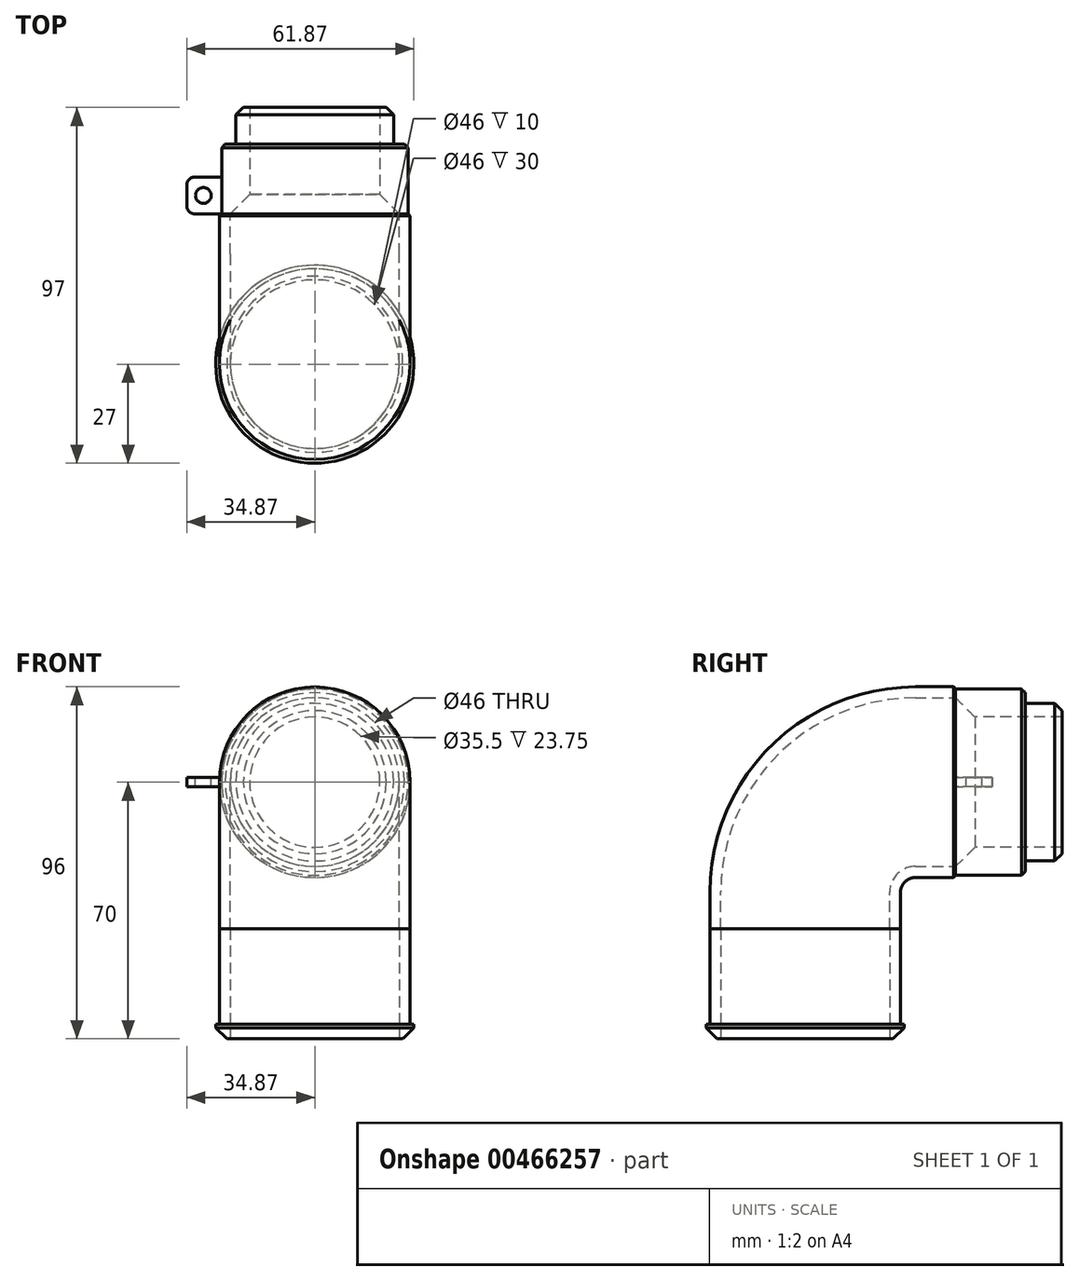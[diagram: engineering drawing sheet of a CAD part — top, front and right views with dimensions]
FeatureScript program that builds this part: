
annotation { "Feature Type Name" : "Feature", "Feature Type Description" : "" }
export const myFeature = defineFeature(function(context is Context, id is Id, definition is map)
    precondition{}
    {
        {
            assignVariable(context, id + "F0", {"name" : "Cyclone_OD", "anyValue" : 52});
        }
        {
            assignVariable(context, id + "F1", {"name" : "Cyclone_ID", "anyValue" : getVariable(context, 'Cyclone_OD') - 6});
        }
        {
            assignVariable(context, id + "F2", {"name" : "CentralVac_ID", "anyValue" : 35.5});
        }
        {
            assignVariable(context, id + "F3", {"name" : "CentralVac_OD1", "anyValue" : 50.8});
        }
        {
            var Q0;
            Q0=qCreatedBy(makeId("Top.planeOp"),FACE);
            var sketch = newSketch(context, id + "F4", { "sketchPlane" : qUnion([Q0])});
            skCircle(sketch, "E0", {"center": v(0, 0) * mm, "radius": 23 * mm});
            skCircle(sketch, "E1", {"center": v(0, 0) * mm, "radius": 26 * mm});
            skSolve(sketch);
        }
        {
            var Q0;
            Q0 = qSketchRegion(id + "F4", true);
            extrude(context, id + "F5", {"entities" : qUnion([Q0]), "depth" : 30 * mm});
        }
        {
            var Q0;
            Q0=makeQuery(id+"F5.opExtrude","CAP_FACE",FACE,{"disambiguationData":[OSD([sQuery(id+"F4.wireOp",EDGE,"E0"),sQuery(id+"F4.wireOp",EDGE,"E1")])],"isStart":true});
            var sketch = newSketch(context, id + "F6", { "sketchPlane" : qUnion([Q0])});
            skCircle(sketch, "E2", {"center": v(0, 0) * mm, "radius": 26 * mm});
            skCircle(sketch, "E3", {"center": v(0, 0) * mm, "radius": 27 * mm});
            skSolve(sketch);
        }
        {
            var Q0;
            Q0 = qSketchRegion(id + "F6", true);
            extrude(context, id + "F7", {"entities" : qUnion([Q0]), "operationType" : NewBodyOperationType.ADD, "depth" : -4 * mm});
        }
        {
            var Q0;
            Q0=makeQuery(id+"F7.opExtrude","CAP_EDGE",EDGE,{"disambiguationData":[OSD([sQuery(id+"F6.wireOp",EDGE,"E3")])],"isStart":true});
            chamfer(context, id + "F8", {"entities" : qUnion([Q0]), "width" : 3 * mm, "tangentPropagation" : true});
        }
        {
            var Q0;
            Q0=qCreatedBy(makeId("Right.planeOp"),FACE);
            var sketch = newSketch(context, id + "F9", { "sketchPlane" : qUnion([Q0])});
            skLineSegment(sketch, "E4", {"start": v(41, 70) * mm, "end": v(41, 30) * mm, "construction": true});
            skLineSegment(sketch, "E5", {"start": v(41, 30) * mm, "end": v(26, 30) * mm, "construction": true});
            skLineSegment(sketch, "E6", {"start": v(41, 70) * mm, "end": v(30, 70) * mm});
            skLineSegment(sketch, "E7", {"start": v(0, 40) * mm, "end": v(0, 30) * mm});
            skPoint(sketch, "E8.visualSharp", {"position": v(0, 70) * mm});
            skArc(sketch, "E8.filletArc", {"start": v(30, 70) * mm, "mid": v(8.79, 61.21) * mm, "end": v(0, 40) * mm});
            skSolve(sketch);
        }
        {
            var Q0;
            Q0=makeQuery(id+"F5.opExtrude","CAP_FACE",FACE,{"disambiguationData":[OSD([sQuery(id+"F4.wireOp",EDGE,"E0"),sQuery(id+"F4.wireOp",EDGE,"E1")])],"isStart":false});
            var sketch = newSketch(context, id + "F10", { "sketchPlane" : qUnion([Q0])});
            skCircle(sketch, "E9", {"center": v(0, 0) * mm, "radius": 23 * mm});
            skCircle(sketch, "E10", {"center": v(0, 0) * mm, "radius": 26 * mm});
            skSolve(sketch);
        }
        {
            var Q0;
            Q0 = qSketchRegion(id + "F10", true);
            var Q1;
            Q1 = qConstructionFilter(qBodyType(qCreatedBy(id + "F9" ,EDGE), BodyType.WIRE), ConstructionObject.NO);
            sweep(context, id + "F11", {"profiles" : qUnion([Q0]), "path" : qUnion([Q1])});
        }
        {
            var Q0;
            Q0=makeQuery(id+"F11.opSweep","CAP_FACE",FACE,{"disambiguationData":[OSD([sQuery(id+"F9.wireOp",VERTEX,"E6.start"),sQuery(id+"F10.wireOp",EDGE,"E9"),sQuery(id+"F10.wireOp",EDGE,"E10")])],"isStart":false});
            var sketch = newSketch(context, id + "F12", { "sketchPlane" : qUnion([Q0])});
            skCircle(sketch, "E11", {"center": v(0, 70) * mm, "radius": 25.4 * mm});
            skCircle(sketch, "E12", {"center": v(0, 70) * mm, "radius": 17.75 * mm});
            skSolve(sketch);
        }
        {
            var Q0;
            Q0 = qSketchRegion(id + "F12", true);
            extrude(context, id + "F13", {"entities" : qUnion([Q0]), "depth" : 19 * mm});
        }
        {
            var Q0;
            Q0=makeQuery(id+"F13.opExtrude","CAP_FACE",FACE,{"disambiguationData":[OSD([sQuery(id+"F12.wireOp",EDGE,"E11"),sQuery(id+"F12.wireOp",EDGE,"E12")])],"isStart":false});
            var sketch = newSketch(context, id + "F14", { "sketchPlane" : qUnion([Q0])});
            skCircle(sketch, "E13", {"center": v(0, 70) * mm, "radius": 17.75 * mm});
            skCircle(sketch, "E14", {"center": v(0, 70) * mm, "radius": 21.5 * mm});
            skSolve(sketch);
        }
        {
            var Q0;
            Q0 = qSketchRegion(id + "F14", true);
            extrude(context, id + "F15", {"entities" : qUnion([Q0]), "operationType" : NewBodyOperationType.ADD, "depth" : 10 * mm});
        }
        {
            var Q0;
            Q0=makeQuery(id+"F13.opExtrude","CAP_EDGE",EDGE,{"disambiguationData":[OSD([sQuery(id+"F12.wireOp",EDGE,"E12")])],"isStart":true});
            chamfer(context, id + "F16", {"entities" : qUnion([Q0]), "width" : ((getVariable(context, 'Cyclone_ID') - getVariable(context, 'CentralVac_ID')) / 2) * mm, "tangentPropagation" : true});
        }
        {
            var Q0;
            Q0=makeQuery(id+"F11.opSweep","CAP_EDGE",EDGE,{"disambiguationData":[OSD([sQuery(id+"F9.wireOp",VERTEX,"E6.start"),sQuery(id+"F10.wireOp",EDGE,"E10")])],"isStart":false});
            chamfer(context, id + "F17", {"entities" : qUnion([Q0]), "width" : ((getVariable(context, 'Cyclone_OD') - getVariable(context, 'CentralVac_OD1')) / 2) * mm, "tangentPropagation" : true});
        }
        {
            var Q0;
            Q0=makeQuery(id+"F15.opExtrude","CAP_EDGE",EDGE,{"disambiguationData":[OSD([sQuery(id+"F14.wireOp",EDGE,"E14")])],"isStart":false});
            chamfer(context, id + "F18", {"entities" : qUnion([Q0]), "width" : 2 * mm, "tangentPropagation" : true});
        }
        {
            var Q0;
            Q0=makeQuery(id+"F13.opExtrude","CAP_EDGE",EDGE,{"disambiguationData":[OSD([sQuery(id+"F12.wireOp",EDGE,"E11")])],"isStart":false});
            chamfer(context, id + "F19", {"entities" : qUnion([Q0]), "width" : 1 * mm, "tangentPropagation" : true});
        }
        {
            var Q0;
            Q0=makeQuery(id+"F13.opExtrude","CAP_FACE",FACE,{"disambiguationData":[OSD([sQuery(id+"F12.wireOp",EDGE,"E11"),sQuery(id+"F12.wireOp",EDGE,"E12")])],"isStart":true});
            var sketch = newSketch(context, id + "F20", { "sketchPlane" : qUnion([Q0])});
            skLineSegment(sketch, "E15.bottom", {"start": v(-34.87, 68.75) * mm, "end": v(-25.37, 68.75) * mm});
            skLineSegment(sketch, "E15.top", {"start": v(-34.87, 71.25) * mm, "end": v(-25.37, 71.25) * mm});
            skLineSegment(sketch, "E15.left", {"start": v(-34.87, 68.75) * mm, "end": v(-34.87, 71.25) * mm});
            skLineSegment(sketch, "E15.right", {"start": v(-25.37, 68.75) * mm, "end": v(-25.37, 71.25) * mm});
            skSolve(sketch);
        }
        {
            var Q0;
            Q0 = qSketchRegion(id + "F20", true);
            extrude(context, id + "F21", {"entities" : qUnion([Q0]), "operationType" : NewBodyOperationType.ADD, "depth" : -10 * mm});
        }
        {
            var Q0;
            Q0=makeQuery(id+"F21.opExtrude","SWEPT_FACE",FACE,{"disambiguationData":[OSD([sQuery(id+"F20.wireOp",EDGE,"E15.top")])]});
            var sketch = newSketch(context, id + "F22", { "sketchPlane" : qUnion([Q0])});
            skCircle(sketch, "E16", {"center": v(-30.37, 46) * mm, "radius": 2.15 * mm});
            skSolve(sketch);
        }
        {
            var Q0;
            Q0 = qSketchRegion(id + "F22", true);
            extrude(context, id + "F23", {"entities" : qUnion([Q0]), "operationType" : NewBodyOperationType.REMOVE, "endBound" : BoundingType.UP_TO_NEXT, "oppositeDirection" : true, "depth" : 25 * mm});
        }
        {
            var Q0;
            Q0=makeQuery(id+"F21.opExtrude","CAP_EDGE",EDGE,{"disambiguationData":[OSD([sQuery(id+"F20.wireOp",EDGE,"E15.left")])],"isStart":false});
            var Q1;
            Q1=makeQuery(id+"F21.opExtrude","CAP_EDGE",EDGE,{"disambiguationData":[OSD([sQuery(id+"F20.wireOp",EDGE,"E15.left")])],"isStart":true});
            fillet(context, id + "F24", {"entities" : qUnion([Q0, Q1]), "radius" : 2 * mm, "tangentPropagation" : true, "allowEdgeOverflow" : false});
        }
    });
